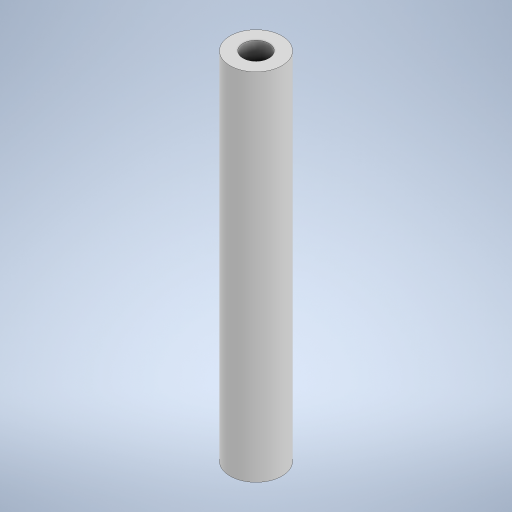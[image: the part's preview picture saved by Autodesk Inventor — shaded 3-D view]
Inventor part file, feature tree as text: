
AUTODESK INVENTOR PART (.ipt)
format: ipt  version: 2024.2 (Build 282272000, 272)  size: 247,808 bytes
history: native  units: mm
features: extrude x3, sketch x3
ambient origin geometry x8: Origin, YZ Plane, XZ Plane, XY Plane, X Axis, Y Axis, Z Axis, Center Point
bodies: Solid1 (feature_tree)
feature tree (6):
  extrude  "Extrusion1"  Depth=5.2mm
  extrude  "Extrusion2"  Depth=5.0mm
  extrude  "Extrusion3"  Depth=50.0mm TaperAngle=0.0deg
  sketch  "Sketch1"  dims[d0=8.0mm d1=5.2mm]
  sketch  "Sketch2"  dims[d2=5.0mm d3=0.0mm d4=3.0mm]
  sketch  "Sketch3"  dims[d5=8.0mm d6=50.0mm d7=0.0mm d8=4.0mm d9=5.0mm d10=0.0mm]
